# Revit family: Body_Spray-Square-GROHE-Rainshower-26845_Series
name_source: partatom
category: Plumbing Fixtures
units: mm (PartAtom-declared; Revit-internal decimal feet)

## family parameters
Cut with Voids When Loaded = No
Host = Face
OmniClass Number = 23.45.05.14.21.11
OmniClass Title = Bath/Shower Units
Part Type = Normal
Room Calculation Point = No
Round Connector Dimension = Use Diameter
Shared = Yes

## types (5) — shared parameters
CEC Compliant = Yes
CW Connection = No
CWFU = 3
CalGreen Compliant = Yes
Default Elevation = 0"
Description = Rainshower™ Body spray- 2 Sprays
Flow Rate = 0.9gpm (3.3L/min)
HW Connection = No
HWFU = 3
Height = 2 15/16"
Installation Type = Wall Mounted
Length = 7/8"
Manufacturer = Grohe
Orifice Material = Rubber-Grohe-White
Price = Prices may vary. Please consult Manufacturer Representative for most up-to-date price list.
Product Documentation Link = https://lixil.cdn.celum.cloud
Product Page URL = https://www.grohe.us
Tempered Connection = Yes
Tempered Water Connection Diameter = 1/2"
URL = https://www.grohe.us
Vent Connection = No
WFU = 4
Waste Connection = No
Width = 2 15/16"

## per-type parameters (varying)
| type | Assembly Code | Finish | IAPMO Compliance | Material |
| 26845000 | D2010510 | Metal-Grohe-000-StarLight Chrome | • Massachusetts Plumbing Board Approved  • CSA B125.1 • ASME A112.18.1 | Metal-Grohe-000-StarLight Chrome |
| 268452430 | D2010510 | Metal-Grohe-2430-Matte Black | • Massachusetts Plumbing Board Approved  • CSA B125.1 • ASME A112.18.1 | Metal-Grohe-2430-Matte Black |
| 26845EN0 | D2010510 | Metal-Grohe-EN0-Brushed Nickel Infinity Finish | • Massachusetts Plumbing Board Approved  • CSA B125.1 • ASME A112.18.1 | Metal-Grohe-EN0-Brushed Nickel Infinity Finish |
| 26845GN0 | D2010710 | Metal-Grohe-GN0-Brushed Cool Sunrise | • Massachusetts Plumbing Board Approved • Energy Policy Act of 1992 • CSA B125.1 • ASME A112.18.1 | Metal-Grohe-GN0-Brushed Cool Sunrise |
| 26845A00 | D2010510 | Metal-Grohe-A00-Hard Graphite | • Massachusetts Plumbing Board Approved  • CSA B125.1 • ASME A112.18.1 | Metal-Grohe-A00-Hard Graphite |

note: column(s) folded — value = type name in every type: Model

## geometry (parser evidence)
native form markers: Sweep x2
no freeform markers — native parametric forms only
